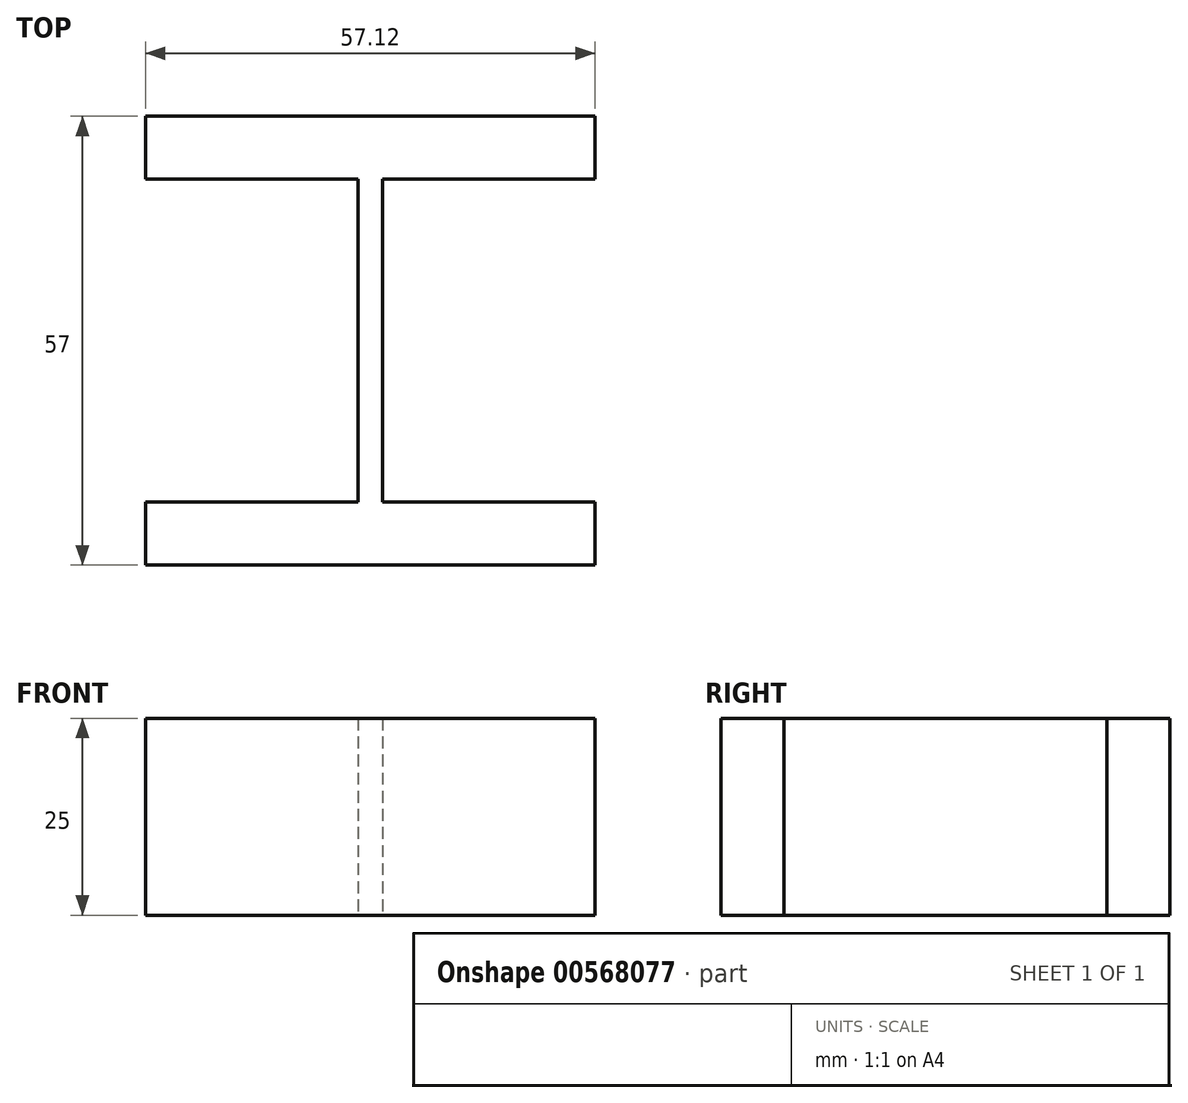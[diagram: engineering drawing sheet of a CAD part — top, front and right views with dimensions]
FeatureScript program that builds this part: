
annotation { "Feature Type Name" : "Feature", "Feature Type Description" : "" }
export const myFeature = defineFeature(function(context is Context, id is Id, definition is map)
    precondition{}
    {
        {
            var Q0;
            Q0=qCreatedBy(makeId("Top.planeOp"),FACE);
            var sketch = newSketch(context, id + "F0", { "sketchPlane" : qUnion([Q0])});
            skLineSegment(sketch, "E0", {"start": v(-46.51, 63.6) * mm, "end": v(-46.51, 55.6) * mm});
            skLineSegment(sketch, "E1", {"start": v(-46.51, 63.6) * mm, "end": v(10.6, 63.6) * mm});
            skLineSegment(sketch, "E2", {"start": v(10.6, 63.6) * mm, "end": v(10.6, 55.6) * mm});
            skLineSegment(sketch, "E3", {"start": v(10.6, 55.6) * mm, "end": v(-16.4, 55.6) * mm});
            skLineSegment(sketch, "E4", {"start": v(-16.4, 55.6) * mm, "end": v(-16.4, 14.6) * mm});
            skLineSegment(sketch, "E5", {"start": v(-46.51, 55.6) * mm, "end": v(-19.51, 55.6) * mm});
            skLineSegment(sketch, "E6", {"start": v(-19.51, 55.6) * mm, "end": v(-19.51, 14.6) * mm});
            skLineSegment(sketch, "E7", {"start": v(-19.51, 14.6) * mm, "end": v(-46.51, 14.6) * mm});
            skLineSegment(sketch, "E8", {"start": v(-46.51, 14.6) * mm, "end": v(-46.51, 6.6) * mm});
            skLineSegment(sketch, "E9", {"start": v(10.6, 6.6) * mm, "end": v(10.6, 14.6) * mm});
            skLineSegment(sketch, "E10", {"start": v(10.6, 14.6) * mm, "end": v(-16.4, 14.6) * mm});
            skLineSegment(sketch, "E11", {"start": v(-46.51, 6.6) * mm, "end": v(10.6, 6.6) * mm});
            skSolve(sketch);
        }
        {
            var Q0;
            Q0=makeQuery(id+"F0.imprint","IMPRINT",FACE,{"disambiguationData":[TD([[makeQuery(id+"F0.imprint","IMPRINT",EDGE,{"derivedFrom":sQuery(id+"F0.wireOp",EDGE,"E0")}),1.0]])]});
            extrude(context, id + "F1", {"entities" : qUnion([Q0]), "depth" : 25 * mm, "offsetDistance" : 25 * mm});
        }
    });
